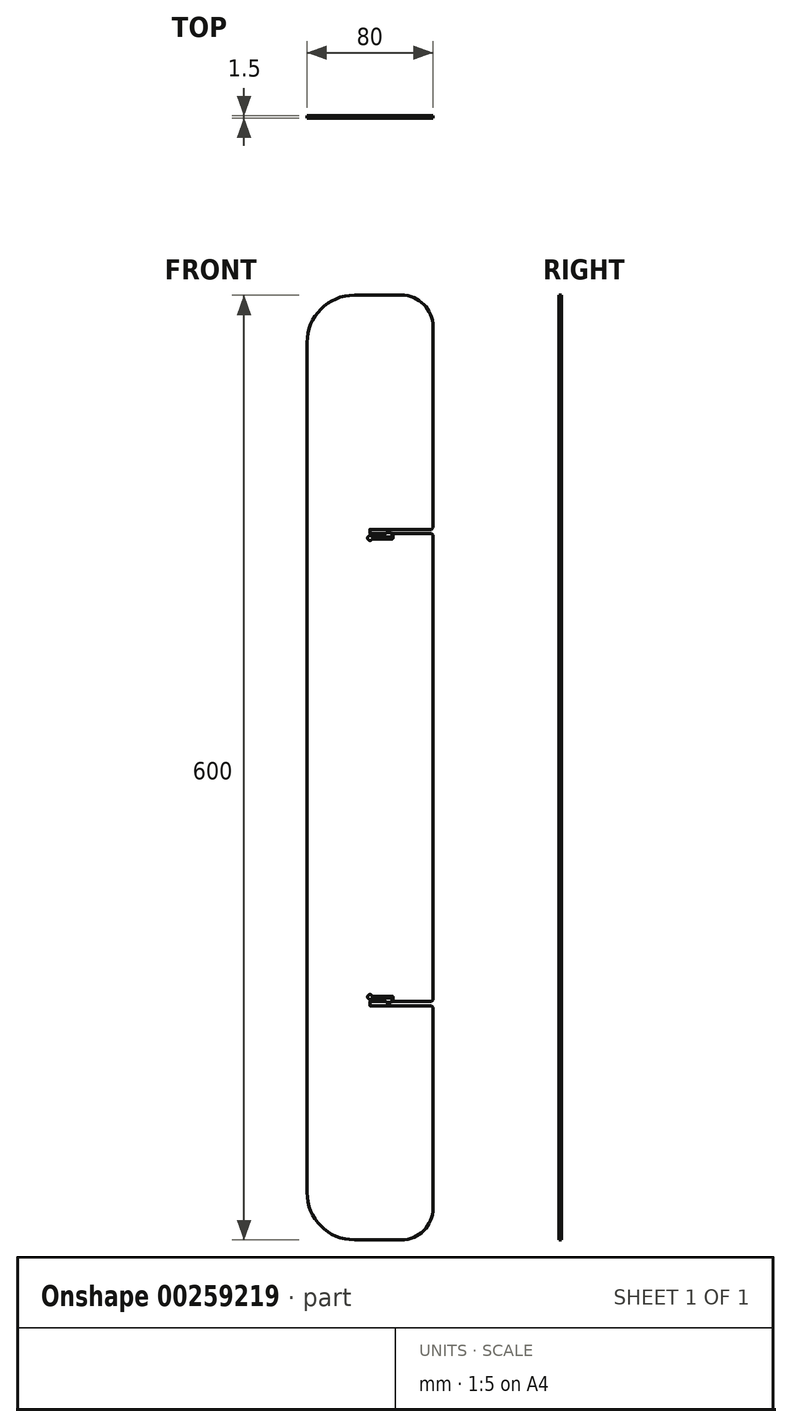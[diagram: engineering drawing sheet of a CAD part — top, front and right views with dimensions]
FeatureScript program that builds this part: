
annotation { "Feature Type Name" : "Feature", "Feature Type Description" : "" }
export const myFeature = defineFeature(function(context is Context, id is Id, definition is map)
    precondition{}
    {
        {
            var Q0;
            Q0=qCreatedBy(makeId("Front.planeOp"),FACE);
            var sketch = newSketch(context, id + "F0", { "sketchPlane" : qUnion([Q0])});
            skLineSegment(sketch, "E0.0", {"start": v(0.1, 1.27) * mm, "end": v(3, 1.27) * mm});
            skLineSegment(sketch, "E1.0", {"start": v(3.2, 1.47) * mm, "end": v(9.8, 1.47) * mm});
            skArc(sketch, "E2.0.0", {"start": v(1.41, 3.75) * mm, "mid": v(0.87, 3.03) * mm, "end": v(0, 2.75) * mm});
            skLineSegment(sketch, "E2.0.3", {"start": v(3, 1.27) * mm, "end": v(3.2, 1.47) * mm});
            skLineSegment(sketch, "E2.0.7", {"start": v(10.13, 0.78) * mm, "end": v(13.05, 0.78) * mm});
            skLineSegment(sketch, "E3.0.6", {"start": v(9.99, 1.33) * mm, "end": v(10.13, 0.78) * mm});
            skArc(sketch, "E3.0.8", {"start": v(13.05, 0.78) * mm, "mid": v(13.13, 0.8) * mm, "end": v(13.2, 0.83) * mm});
            skLineSegment(sketch, "E3.0.9", {"start": v(13.2, 0.83) * mm, "end": v(13.94, 1.58) * mm});
            skLineSegment(sketch, "E3.0.11", {"start": v(14, 1.72) * mm, "end": v(14, 3.55) * mm});
            skLineSegment(sketch, "E3.0.13", {"start": v(13.8, 3.75) * mm, "end": v(1.41, 3.75) * mm});
            skArc(sketch, "E4.0.5", {"start": v(9.8, 1.47) * mm, "mid": v(9.91, 1.43) * mm, "end": v(9.99, 1.33) * mm});
            skArc(sketch, "E4.0.10", {"start": v(13.94, 1.58) * mm, "mid": v(13.98, 1.65) * mm, "end": v(14, 1.72) * mm});
            skArc(sketch, "E5.0.6", {"start": v(14.5, 1.47) * mm, "mid": v(14.56, 1.33) * mm, "end": v(14.7, 1.28) * mm});
            skLineSegment(sketch, "E5.0.13", {"start": v(40, -130) * mm, "end": v(40, -2.27) * mm});
            skLineSegment(sketch, "E6.0.0", {"start": v(0, 0) * mm, "end": v(0, 1.17) * mm});
            skLineSegment(sketch, "E6.0.16", {"start": v(0, -1.18) * mm, "end": v(0, 0) * mm});
            skArc(sketch, "E7.0.2", {"start": v(0, 2.75) * mm, "mid": v(-1.22, 5.12) * mm, "end": v(1.41, 4.75) * mm});
            skLineSegment(sketch, "E7.0.3", {"start": v(1.41, 4.75) * mm, "end": v(14.3, 4.75) * mm});
            skLineSegment(sketch, "E7.0.5", {"start": v(14.5, 4.55) * mm, "end": v(14.5, 1.47) * mm});
            skLineSegment(sketch, "E8", {"start": v(-4.63, 0) * mm, "end": v(42.86, 0) * mm, "construction": true});
            skPoint(sketch, "E9", {"position": v(10, 1.28) * mm});
            skLineSegment(sketch, "E10", {"start": v(-40, -120) * mm, "end": v(-40, 420) * mm});
            skLineSegment(sketch, "E11", {"start": v(-47.13, 150) * mm, "end": v(117.4, 150) * mm, "construction": true});
            skLineSegment(sketch, "E12", {"start": v(-10, -150) * mm, "end": v(20, -150) * mm});
            skLineSegment(sketch, "E13.trimOffspring", {"start": v(40, 150) * mm, "end": v(40, 2.27) * mm});
            skPoint(sketch, "E14.visualSharp", {"position": v(-40, 450) * mm});
            skArc(sketch, "E14.filletArc", {"start": v(-10, 450) * mm, "mid": v(-31.21, 441.21) * mm, "end": v(-40, 420) * mm});
            skPoint(sketch, "E15.visualSharp", {"position": v(-40, -150) * mm});
            skArc(sketch, "E15.filletArc", {"start": v(-40, -120) * mm, "mid": v(-31.21, -141.21) * mm, "end": v(-10, -150) * mm});
            skPoint(sketch, "E16.visualSharp", {"position": v(40, -150) * mm});
            skArc(sketch, "E16.filletArc", {"start": v(20, -150) * mm, "mid": v(34.14, -144.14) * mm, "end": v(40, -130) * mm});
            skArc(sketch, "E17", {"start": v(0.1, 1.27) * mm, "mid": v(-0.07, 1.35) * mm, "end": v(0, 1.17) * mm});
            skArc(sketch, "E18", {"start": v(0, -1.18) * mm, "mid": v(-0.07, -1.35) * mm, "end": v(0.1, -1.28) * mm});
            skPoint(sketch, "E19.orphan", {"position": v(0, 0.75) * mm});
            skLineSegment(sketch, "E20", {"start": v(0, 150) * mm, "end": v(0, -170.54) * mm, "construction": true});
            skPoint(sketch, "E21", {"position": v(0, 0) * mm});
            skCircle(sketch, "E22", {"center": v(0, 0) * mm, "radius": 1.27 * mm, "construction": true});
            skPoint(sketch, "E23.newPointA", {"position": v(14.3, 4.75) * mm});
            skArc(sketch, "E23.filletArc", {"start": v(14.5, 4.55) * mm, "mid": v(14.44, 4.7) * mm, "end": v(14.3, 4.75) * mm});
            skPoint(sketch, "E24.newPointA", {"position": v(13.8, 3.75) * mm});
            skArc(sketch, "E24.filletArc", {"start": v(14, 3.55) * mm, "mid": v(13.94, 3.7) * mm, "end": v(13.8, 3.75) * mm});
            skArc(sketch, "E25.MirrorCS", {"start": v(0.1, 298.73) * mm, "mid": v(-0.07, 298.65) * mm, "end": v(0, 298.82) * mm});
            skArc(sketch, "E26.MirrorCS", {"start": v(0, 301.18) * mm, "mid": v(-0.07, 301.35) * mm, "end": v(0.1, 301.28) * mm});
            skCircle(sketch, "E27.MirrorC", {"center": v(0, 300) * mm, "radius": 1.27 * mm, "construction": true});
            skArc(sketch, "E28.MirrorCS", {"start": v(14, 296.45) * mm, "mid": v(13.94, 296.3) * mm, "end": v(13.8, 296.25) * mm});
            skLineSegment(sketch, "E29.MirrorCS", {"start": v(0, 300) * mm, "end": v(0, 298.82) * mm});
            skLineSegment(sketch, "E30.MirrorCS", {"start": v(0, 301.17) * mm, "end": v(0, 300) * mm});
            skArc(sketch, "E31.MirrorCS", {"start": v(14.5, 295.45) * mm, "mid": v(14.44, 295.3) * mm, "end": v(14.3, 295.25) * mm});
            skLineSegment(sketch, "E32.MirrorCS", {"start": v(14.5, 295.45) * mm, "end": v(14.5, 298.52) * mm});
            skLineSegment(sketch, "E33.MirrorCS", {"start": v(14, 298.28) * mm, "end": v(14, 296.45) * mm});
            skArc(sketch, "E34.MirrorCS", {"start": v(9.8, 298.52) * mm, "mid": v(9.91, 298.57) * mm, "end": v(9.99, 298.67) * mm});
            skLineSegment(sketch, "E35.MirrorCS", {"start": v(9.99, 298.67) * mm, "end": v(10.13, 299.22) * mm});
            skLineSegment(sketch, "E36.MirrorCS", {"start": v(0.1, 298.73) * mm, "end": v(3, 298.73) * mm});
            skLineSegment(sketch, "E37.MirrorCS", {"start": v(10.13, 299.22) * mm, "end": v(13.05, 299.22) * mm});
            skArc(sketch, "E38.MirrorCS", {"start": v(14.5, 298.52) * mm, "mid": v(14.56, 298.67) * mm, "end": v(14.7, 298.72) * mm});
            skLineSegment(sketch, "E39.MirrorCS", {"start": v(13.2, 299.17) * mm, "end": v(13.94, 298.42) * mm});
            skLineSegment(sketch, "E40.MirrorCS", {"start": v(3, 298.72) * mm, "end": v(3.2, 298.52) * mm});
            skArc(sketch, "E41.MirrorCS", {"start": v(13.05, 299.22) * mm, "mid": v(13.13, 299.2) * mm, "end": v(13.2, 299.17) * mm});
            skArc(sketch, "E42.MirrorCS", {"start": v(13.94, 298.42) * mm, "mid": v(13.98, 298.35) * mm, "end": v(14, 298.28) * mm});
            skArc(sketch, "E43.MirrorCS", {"start": v(1.41, 296.25) * mm, "mid": v(0.87, 296.97) * mm, "end": v(0, 297.25) * mm});
            skLineSegment(sketch, "E44.MirrorCS", {"start": v(3.2, 298.52) * mm, "end": v(9.8, 298.52) * mm});
            skPoint(sketch, "E45.MirrorP", {"position": v(0, 299.25) * mm});
            skPoint(sketch, "E46.MirrorP", {"position": v(14.3, 295.25) * mm});
            skLineSegment(sketch, "E47.MirrorCS", {"start": v(-4.63, 300) * mm, "end": v(42.86, 300) * mm, "construction": true});
            skArc(sketch, "E48.MirrorCS", {"start": v(0, 297.25) * mm, "mid": v(-1.22, 294.88) * mm, "end": v(1.41, 295.25) * mm});
            skPoint(sketch, "E49.MirrorP", {"position": v(10, 298.72) * mm});
            skPoint(sketch, "E50.MirrorP", {"position": v(13.8, 296.25) * mm});
            skLineSegment(sketch, "E51.MirrorCS", {"start": v(13.8, 296.25) * mm, "end": v(1.41, 296.25) * mm});
            skLineSegment(sketch, "E52.MirrorCS", {"start": v(1.41, 295.25) * mm, "end": v(14.3, 295.25) * mm});
            skPoint(sketch, "E53.orphan", {"position": v(0, 6.6) * mm});
            skPoint(sketch, "E54.orphan", {"position": v(0, -2.3) * mm});
            skLineSegment(sketch, "E55.MirrorCS", {"start": v(0, 150) * mm, "end": v(0, 470.54) * mm, "construction": true});
            skLineSegment(sketch, "E56", {"start": v(14.7, -1.28) * mm, "end": v(0, -1.28) * mm});
            skLineSegment(sketch, "E57.MirrorCS", {"start": v(14.7, 301.28) * mm, "end": v(0, 301.28) * mm});
            skLineSegment(sketch, "E58.MirrorCS", {"start": v(40, 430) * mm, "end": v(40, 302.27) * mm});
            skLineSegment(sketch, "E59.MirrorCS", {"start": v(40, 150) * mm, "end": v(40, 297.73) * mm});
            skLineSegment(sketch, "E60", {"start": v(40, 2.27) * mm, "end": v(39, 1.27) * mm});
            skLineSegment(sketch, "E61", {"start": v(34.22, 2.27) * mm, "end": v(51.38, 2.27) * mm, "construction": true});
            skLineSegment(sketch, "E62", {"start": v(34.5, 1.27) * mm, "end": v(52.1, 1.27) * mm, "construction": true});
            skLineSegment(sketch, "E63", {"start": v(14.7, 1.28) * mm, "end": v(39, 1.27) * mm});
            skLineSegment(sketch, "E64.MirrorCS", {"start": v(14.7, -1.28) * mm, "end": v(39, -1.27) * mm});
            skLineSegment(sketch, "E65.MirrorCS", {"start": v(40, -2.27) * mm, "end": v(39, -1.27) * mm});
            skLineSegment(sketch, "E66.MirrorCS", {"start": v(14.7, 298.73) * mm, "end": v(39, 298.73) * mm});
            skLineSegment(sketch, "E67.MirrorCS", {"start": v(14.7, 301.28) * mm, "end": v(39, 301.27) * mm});
            skLineSegment(sketch, "E68.MirrorCS", {"start": v(40, 297.73) * mm, "end": v(39, 298.73) * mm});
            skLineSegment(sketch, "E69.MirrorCS", {"start": v(40, 302.27) * mm, "end": v(39, 301.27) * mm});
            skLineSegment(sketch, "E70.MirrorCS", {"start": v(-10, 450) * mm, "end": v(20, 450) * mm});
            skArc(sketch, "E71.MirrorCS", {"start": v(20, 450) * mm, "mid": v(34.14, 444.14) * mm, "end": v(40, 430) * mm});
            skSolve(sketch);
        }
        {
            var Q0;
            Q0=qSketchRegion(id+"F0",true);
            extrude(context, id + "F1", {"entities" : qUnion([Q0]), "depth" : 0.75 * mm, "hasSecondDirection" : true, "secondDirectionOppositeDirection" : true, "secondDirectionDepth" : 0.75 * mm});
        }
    });
